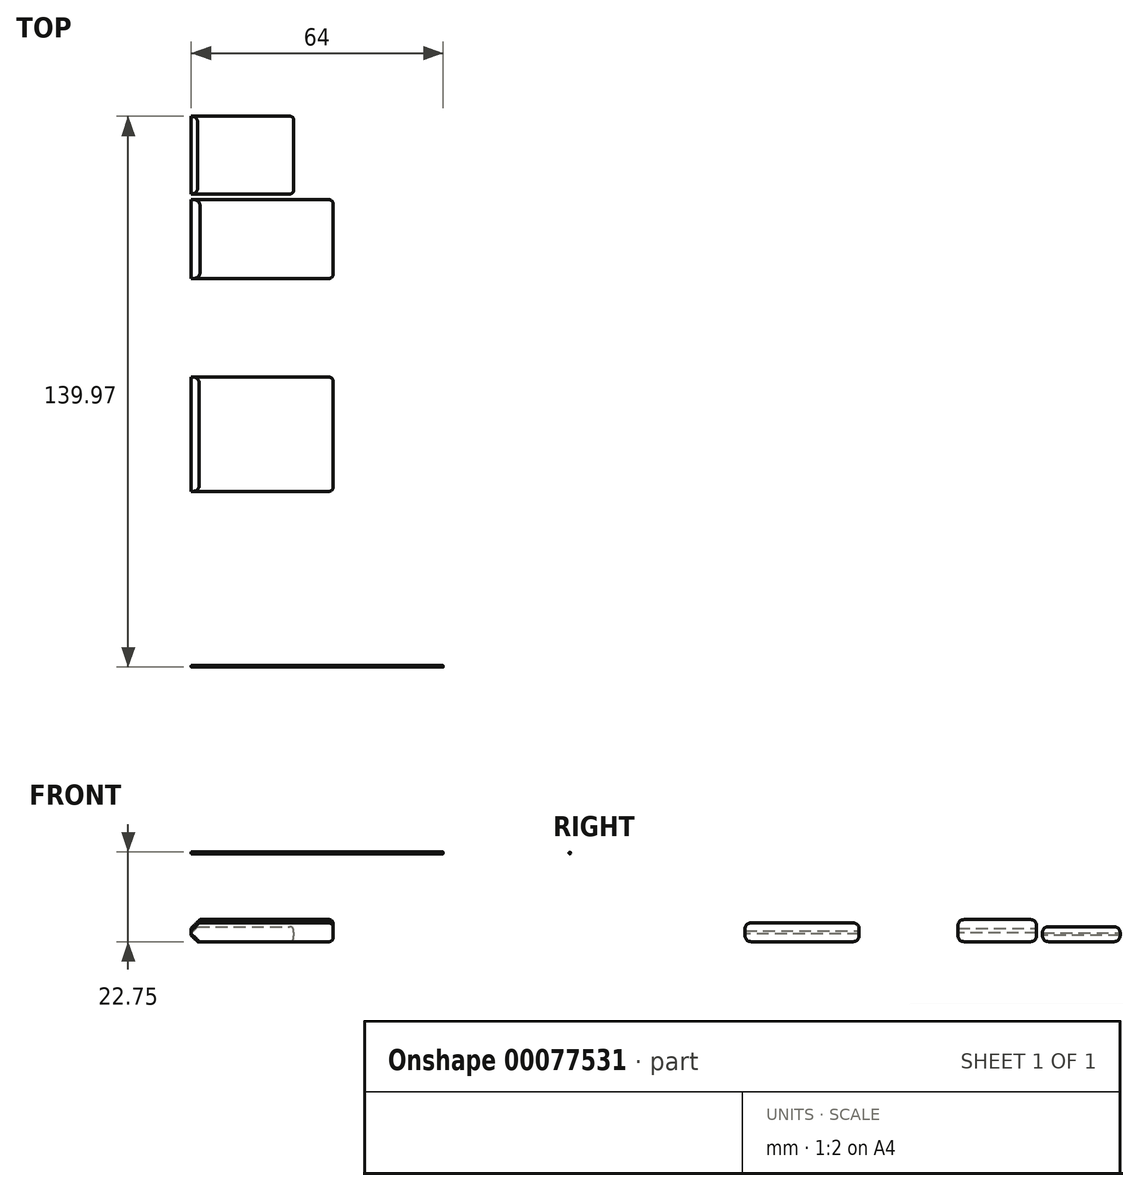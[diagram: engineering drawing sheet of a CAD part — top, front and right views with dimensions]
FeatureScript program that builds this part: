
annotation { "Feature Type Name" : "Feature", "Feature Type Description" : "" }
export const myFeature = defineFeature(function(context is Context, id is Id, definition is map)
    precondition{}
    {
        {
            var Q0;
            Q0=qCreatedBy(makeId("Top.planeOp"),FACE);
            var sketch = newSketch(context, id + "F0", { "sketchPlane" : qUnion([Q0])});
            skLineSegment(sketch, "E0.bottom", {"start": v(0, 0) * mm, "end": v(36, 0) * mm});
            skLineSegment(sketch, "E0.top", {"start": v(0, 29) * mm, "end": v(36, 29) * mm});
            skLineSegment(sketch, "E0.left", {"start": v(0, 0) * mm, "end": v(0, 29) * mm});
            skLineSegment(sketch, "E0.right", {"start": v(36, 0) * mm, "end": v(36, 29) * mm});
            skSolve(sketch);
        }
        {
            var Q0;
            Q0=makeQuery(id+"F0.imprint","IMPRINT",FACE,{"disambiguationData":[TD([[makeQuery(id+"F0.imprint","IMPRINT",EDGE,{"derivedFrom":sQuery(id+"F0.wireOp",EDGE,"E0.bottom")}),1.0]])]});
            extrude(context, id + "F1", {"entities" : qUnion([Q0]), "depth" : 4.75 * mm});
        }
        {
            var Q0;
            Q0=makeQuery(id+"F1.opExtrude","CAP_EDGE",EDGE,{"disambiguationData":[OSD([sQuery(id+"F0.wireOp",EDGE,"E0.bottom")])],"isStart":false});
            var Q1;
            Q1=makeQuery(id+"F1.opExtrude","CAP_EDGE",EDGE,{"disambiguationData":[OSD([sQuery(id+"F0.wireOp",EDGE,"E0.bottom")])],"isStart":true});
            var Q2;
            Q2=makeQuery(id+"F1.opExtrude","CAP_EDGE",EDGE,{"disambiguationData":[OSD([sQuery(id+"F0.wireOp",EDGE,"E0.top")])],"isStart":false});
            var Q3;
            Q3=makeQuery(id+"F1.opExtrude","CAP_EDGE",EDGE,{"disambiguationData":[OSD([sQuery(id+"F0.wireOp",EDGE,"E0.top")])],"isStart":true});
            fillet(context, id + "F2", {"entities" : qUnion([Q0, Q1, Q2, Q3]), "radius" : 1.5 * mm, "tangentPropagation" : true, "allowEdgeOverflow" : false});
        }
        {
            var Q0;
            Q0=makeQuery(id+"F1.opExtrude","CAP_EDGE",EDGE,{"disambiguationData":[OSD([sQuery(id+"F0.wireOp",EDGE,"E0.left")])],"isStart":true});
            var Q1;
            Q1=makeQuery(id+"F1.opExtrude","CAP_EDGE",EDGE,{"disambiguationData":[OSD([sQuery(id+"F0.wireOp",EDGE,"E0.left")])],"isStart":false});
            chamfer(context, id + "F3", {"entities" : qUnion([Q0, Q1]), "width" : 2 * mm});
        }
        {
            var Q0;
            Q0=makeQuery(id+"F1.opExtrude","CAP_EDGE",EDGE,{"disambiguationData":[OSD([sQuery(id+"F0.wireOp",EDGE,"E0.right")])],"isStart":false});
            var Q1;
            Q1=makeQuery(id+"F1.opExtrude","CAP_EDGE",EDGE,{"disambiguationData":[OSD([sQuery(id+"F0.wireOp",EDGE,"E0.right")])],"isStart":true});
            fillet(context, id + "F4", {"entities" : qUnion([Q0, Q1]), "radius" : 1 * mm, "tangentPropagation" : true, "allowEdgeOverflow" : false});
        }
        {
            var Q0;
            Q0=qCreatedBy(makeId("Top.planeOp"),FACE);
            var sketch = newSketch(context, id + "F5", { "sketchPlane" : qUnion([Q0])});
            skLineSegment(sketch, "E1.bottom", {"start": v(0, 54.08) * mm, "end": v(36, 54.08) * mm});
            skLineSegment(sketch, "E1.top", {"start": v(0, 74.08) * mm, "end": v(36, 74.08) * mm});
            skLineSegment(sketch, "E1.left", {"start": v(0, 54.08) * mm, "end": v(0, 74.08) * mm});
            skLineSegment(sketch, "E1.right", {"start": v(36, 54.08) * mm, "end": v(36, 74.08) * mm});
            skSolve(sketch);
        }
        {
            var Q0;
            Q0 = qSketchRegion(id + "F5", true);
            extrude(context, id + "F6", {"entities" : qUnion([Q0]), "depth" : 5.6 * mm});
        }
        {
            var Q0;
            Q0=makeQuery(id+"F6.opExtrude","CAP_EDGE",EDGE,{"disambiguationData":[OSD([sQuery(id+"F5.wireOp",EDGE,"E1.bottom")])],"isStart":false});
            var Q1;
            Q1=makeQuery(id+"F6.opExtrude","CAP_EDGE",EDGE,{"disambiguationData":[OSD([sQuery(id+"F5.wireOp",EDGE,"E1.bottom")])],"isStart":true});
            var Q2;
            Q2=makeQuery(id+"F6.opExtrude","CAP_EDGE",EDGE,{"disambiguationData":[OSD([sQuery(id+"F5.wireOp",EDGE,"E1.top")])],"isStart":false});
            var Q3;
            Q3=makeQuery(id+"F6.opExtrude","CAP_EDGE",EDGE,{"disambiguationData":[OSD([sQuery(id+"F5.wireOp",EDGE,"E1.top")])],"isStart":true});
            fillet(context, id + "F7", {"entities" : qUnion([Q0, Q1, Q2, Q3]), "radius" : 1.5 * mm, "tangentPropagation" : true, "allowEdgeOverflow" : false});
        }
        {
            var Q0;
            Q0=makeQuery(id+"F6.opExtrude","CAP_EDGE",EDGE,{"disambiguationData":[OSD([sQuery(id+"F5.wireOp",EDGE,"E1.right")])],"isStart":false});
            var Q1;
            Q1=makeQuery(id+"F6.opExtrude","CAP_EDGE",EDGE,{"disambiguationData":[OSD([sQuery(id+"F5.wireOp",EDGE,"E1.right")])],"isStart":true});
            fillet(context, id + "F8", {"entities" : qUnion([Q0, Q1]), "radius" : 1 * mm, "tangentPropagation" : true, "allowEdgeOverflow" : false});
        }
        {
            var Q0;
            Q0=makeQuery(id+"F6.opExtrude","CAP_EDGE",EDGE,{"disambiguationData":[OSD([sQuery(id+"F5.wireOp",EDGE,"E1.left")])],"isStart":false});
            var Q1;
            Q1=makeQuery(id+"F6.opExtrude","CAP_EDGE",EDGE,{"disambiguationData":[OSD([sQuery(id+"F5.wireOp",EDGE,"E1.left")])],"isStart":true});
            chamfer(context, id + "F9", {"entities" : qUnion([Q0, Q1]), "width" : 2.2 * mm});
        }
        {
            var Q0;
            Q0=qCreatedBy(makeId("Top.planeOp"),FACE);
            var sketch = newSketch(context, id + "F10", { "sketchPlane" : qUnion([Q0])});
            skLineSegment(sketch, "E2.bottom", {"start": v(0, 75.54) * mm, "end": v(26.02, 75.54) * mm});
            skLineSegment(sketch, "E2.top", {"start": v(0, 95.3) * mm, "end": v(26.02, 95.3) * mm});
            skLineSegment(sketch, "E2.left", {"start": v(0, 75.54) * mm, "end": v(0, 95.3) * mm});
            skLineSegment(sketch, "E2.right", {"start": v(26.02, 75.54) * mm, "end": v(26.02, 95.3) * mm});
            skSolve(sketch);
        }
        {
            var Q0;
            Q0 = qSketchRegion(id + "F10", true);
            extrude(context, id + "F11", {"entities" : qUnion([Q0]), "depth" : 3.8 * mm});
        }
        {
            var Q0;
            Q0=makeQuery(id+"F11.opExtrude","CAP_EDGE",EDGE,{"disambiguationData":[OSD([sQuery(id+"F10.wireOp",EDGE,"E2.bottom")])],"isStart":false});
            var Q1;
            Q1=makeQuery(id+"F11.opExtrude","CAP_EDGE",EDGE,{"disambiguationData":[OSD([sQuery(id+"F10.wireOp",EDGE,"E2.bottom")])],"isStart":true});
            var Q2;
            Q2=makeQuery(id+"F11.opExtrude","CAP_EDGE",EDGE,{"disambiguationData":[OSD([sQuery(id+"F10.wireOp",EDGE,"E2.top")])],"isStart":false});
            var Q3;
            Q3=makeQuery(id+"F11.opExtrude","CAP_EDGE",EDGE,{"disambiguationData":[OSD([sQuery(id+"F10.wireOp",EDGE,"E2.top")])],"isStart":true});
            fillet(context, id + "F12", {"entities" : qUnion([Q0, Q1, Q2, Q3]), "radius" : 1.5 * mm, "tangentPropagation" : true, "allowEdgeOverflow" : false});
        }
        {
            var Q0;
            Q0=makeQuery(id+"F11.opExtrude","CAP_EDGE",EDGE,{"disambiguationData":[OSD([sQuery(id+"F10.wireOp",EDGE,"E2.right")])],"isStart":false});
            var Q1;
            Q1=makeQuery(id+"F11.opExtrude","CAP_EDGE",EDGE,{"disambiguationData":[OSD([sQuery(id+"F10.wireOp",EDGE,"E2.right")])],"isStart":true});
            fillet(context, id + "F13", {"entities" : qUnion([Q0, Q1]), "radius" : 1 * mm, "tangentPropagation" : true, "allowEdgeOverflow" : false});
        }
        {
            var Q0;
            Q0=makeQuery(id+"F11.opExtrude","CAP_EDGE",EDGE,{"disambiguationData":[OSD([sQuery(id+"F10.wireOp",EDGE,"E2.left")])],"isStart":false});
            var Q1;
            Q1=makeQuery(id+"F11.opExtrude","CAP_EDGE",EDGE,{"disambiguationData":[OSD([sQuery(id+"F10.wireOp",EDGE,"E2.left")])],"isStart":true});
            chamfer(context, id + "F14", {"entities" : qUnion([Q0, Q1]), "width" : 1.6 * mm});
        }
        {
            var Q0;
            Q0=qCreatedBy(makeId("Right.planeOp"),FACE);
            var sketch = newSketch(context, id + "F15", { "sketchPlane" : qUnion([Q0])});
            skCircle(sketch, "E3", {"center": v(-44.48, 22.55) * mm, "radius": 0.2 * mm});
            skSolve(sketch);
        }
        {
            var Q0;
            Q0 = qSketchRegion(id + "F15", true);
            extrude(context, id + "F16", {"entities" : qUnion([Q0]), "depth" : 64 * mm});
        }
    });
